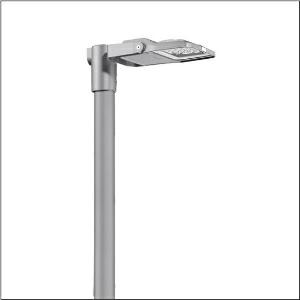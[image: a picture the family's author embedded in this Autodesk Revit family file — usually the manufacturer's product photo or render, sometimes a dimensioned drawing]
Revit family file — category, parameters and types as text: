
# Revit family: floodlight_fl_21_iq_micro___pl61_5xa7762a2c3a_d37b
name_source: partatom
category: Lighting Fixtures
units: mm (PartAtom-declared; Revit-internal decimal feet)

## family parameters
Cut with Voids When Loaded = No
Host = Face
Light Source = No
Part Type = Normal
Room Calculation Point = No
Round Connector Dimension = Use Diameter
Shared = No

## types (1)
- --- (1 x LED, 2910 lm, 23.1 W, 3000K)
    Apparent Load = 23 VA
    CIE Flux Codes = 33 65 98 100 100
    Color Rendering = 70
    Color Temperature = 3000K
    Default Elevation = 1800 mm
    Description = Floodlight FL 21 iQ micro, floodlight, primary light control with lens, of PMMA, primary optical cover: protective disc, of toughened safety glass, transparent, light distribution: PL61, light emission: direct distribution, installation type: surface-mounted, LED, High Power LED, rated luminous flux: 2.910lm, luminous efficacy: 126lm/W, light colour: 730, colour temperature: 3000K, control: Auto-Match, Temp-Guard, Night-Set, Smart-Wire, Desk-Remote (wireless, voltage-free reading and setting of iQ features in the workshop via application-optimized NFC function/RFID function), optimised constant luminous flux control (CLO 2.0), Street-Remote, with terminal, 6-pole, mains connection: 220..240V, AC, 50/60Hz, start of lifetime: 23W, end of service life: 24W, reduction: 11W, luminaire housing, of diecast aluminium, powder-coated, Siteco® metallic grey (DB 702S), corrosivity category C5 mid according to DIN EN ISO 12944, sealing non-destructively replaceable, please order mast flange separately, mast bracket, of steel, galvanised, powder-coated, Siteco® metallic grey (DB 702S), protection rating (complete): IP66, insulation class (complete): insulation class II (safety insulation), certification: CE, ENEC, VDE, protection symbol: D, impact resistance: IK07, permissible operating ambient temperature: -40..+40°C, permissible operating ambient temperature for outdoor applications: -40..+50°C, standard: DIN EN 12944, LABS conformity tested according to VDMA 24364:2018-05, packaging unit: 1 piece

Light Distribution: PL61
    Height = 65 mm
    Lamp = 1 x LED
    Lamp Light Flux = 2910 lm
    Lamp Power = 23.1 W
    Lamp count = 1
    Length = 312 mm
    Luminous efficacy = 126 lm/W
    Manufacturer = Siteco
    ModVariant = No
    Model = 5XA7762A2C3A
    Number of Poles = 1
    OnlyDefault = Yes
    Power Factor = 1
    Product Name = Floodlight FL 21 iQ micro | PL61
    Product group = floodlight | pylon annexe
    ProductGroupID = 6200
    Protection Class = Protection class II
    Protection Degree = IP 66
    RLX_Detail_Level = 1
    RLX_Emergency_Light_Flux = 0 lm
    RLX_Emergency_Type = 0
    RLX_Emergency_Type_DB = No
    RlxData = <blob elided: 101849 chars, md5=554cbcc3>
    Socket = socket
    Standby Power = 0 W
    System Light Flux = 2910 lm
    System Power = 23 W
    Type Comments = factory setting: luminous flux: 100 % | dim-lin: 254 | 455 mA
    Type Image = l_1007121.jpg
    URL = http://relux.com
    VarID = @adj_147013
    Voltage = 0 V
    Weight = 0.00 kg
    Width = 230 mm

## geometry (parser evidence)
native form markers: Blend x4, Sweep x13
no freeform markers — native parametric forms only
